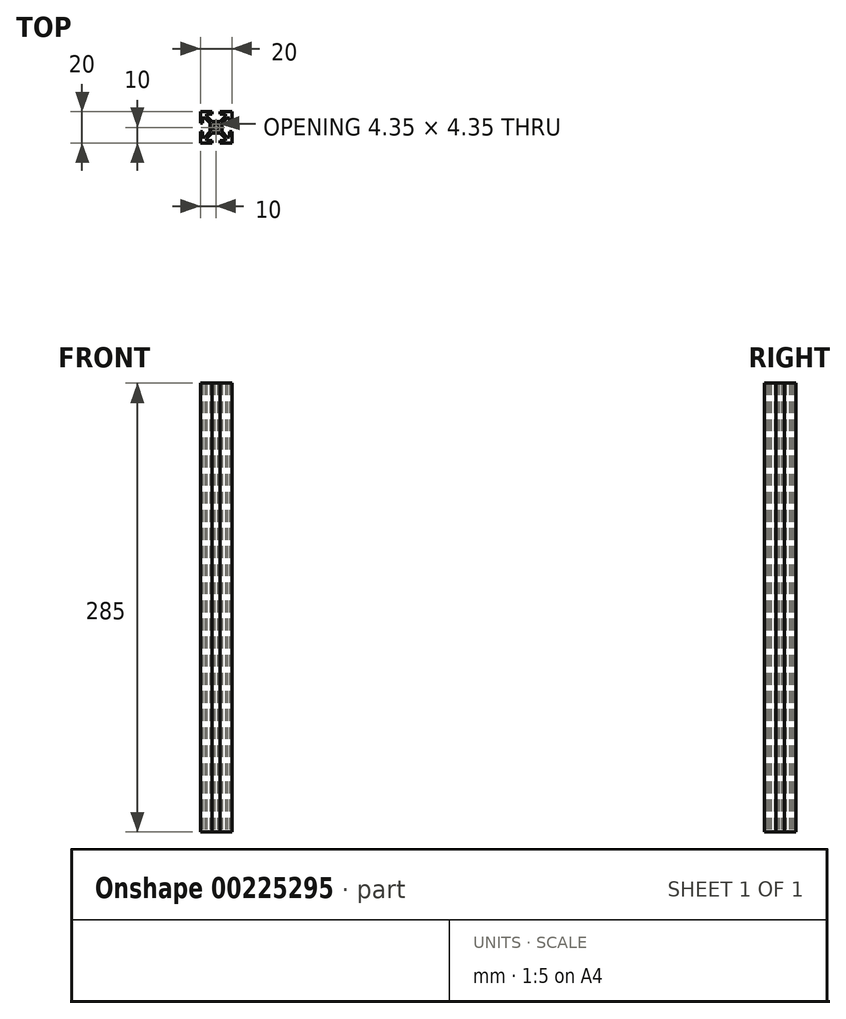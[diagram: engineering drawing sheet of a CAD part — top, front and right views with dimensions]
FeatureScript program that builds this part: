
annotation { "Feature Type Name" : "Feature", "Feature Type Description" : "" }
export const myFeature = defineFeature(function(context is Context, id is Id, definition is map)
    precondition{}
    {
        {
            var Q0;
            Q0=qCreatedBy(makeId("Top.planeOp"),FACE);
            var sketch = newSketch(context, id + "F0", { "sketchPlane" : qUnion([Q0])});
            skLineSegment(sketch, "E0.bottom", {"start": v(10, 10) * mm, "end": v(-10, 10) * mm});
            skLineSegment(sketch, "E0.top", {"start": v(10, -10) * mm, "end": v(-10, -10) * mm});
            skLineSegment(sketch, "E0.left", {"start": v(10, 10) * mm, "end": v(10, -10) * mm});
            skLineSegment(sketch, "E0.right", {"start": v(-10, 10) * mm, "end": v(-10, -10) * mm});
            skPoint(sketch, "E0.middle", {"position": v(0, 0) * mm});
            skLineSegment(sketch, "E1", {"start": v(-10, 10) * mm, "end": v(10, -10) * mm, "construction": true});
            skLineSegment(sketch, "E2", {"start": v(-10, -10) * mm, "end": v(10, 10) * mm, "construction": true});
            skLineSegment(sketch, "E3", {"start": v(0, 10) * mm, "end": v(0, -10) * mm, "construction": true});
            skLineSegment(sketch, "E4", {"start": v(-10, 0) * mm, "end": v(10, 0) * mm, "construction": true});
            skPoint(sketch, "E4.endSnap0", {"position": v(10, 0) * mm});
            skLineSegment(sketch, "E5", {"start": v(-2.63, 13.49) * mm, "end": v(2.63, 13.49) * mm});
            skLineSegment(sketch, "E6", {"start": v(2.63, 13.49) * mm, "end": v(2.63, 8.5) * mm});
            skLineSegment(sketch, "E7", {"start": v(2.63, 8.5) * mm, "end": v(6, 8.5) * mm});
            skLineSegment(sketch, "E8", {"start": v(6, 8.5) * mm, "end": v(6, 7.06) * mm});
            skLineSegment(sketch, "E9", {"start": v(6, 7.06) * mm, "end": v(2.6, 3.66) * mm});
            skLineSegment(sketch, "E10", {"start": v(2.6, 3.66) * mm, "end": v(-2.6, 3.66) * mm});
            skLineSegment(sketch, "E11", {"start": v(-2.6, 3.66) * mm, "end": v(-6, 7.06) * mm});
            skLineSegment(sketch, "E12", {"start": v(-6, 7.06) * mm, "end": v(-6, 8.5) * mm});
            skLineSegment(sketch, "E13", {"start": v(-6, 8.5) * mm, "end": v(-2.63, 8.5) * mm});
            skLineSegment(sketch, "E14", {"start": v(-2.63, 8.5) * mm, "end": v(-2.63, 13.49) * mm});
            skCircle(sketch, "E15", {"center": v(0, 0) * mm, "radius": 2.1 * mm});
            skLineSegment(sketch, "E16.MirrorCS", {"start": v(-7.06, 6) * mm, "end": v(-8.5, 6) * mm});
            skLineSegment(sketch, "E17.MirrorCS", {"start": v(-3.66, 2.6) * mm, "end": v(-7.06, 6) * mm});
            skLineSegment(sketch, "E18.MirrorCS", {"start": v(-8.5, 6) * mm, "end": v(-8.5, 2.63) * mm});
            skLineSegment(sketch, "E19.MirrorCS", {"start": v(-3.66, -2.6) * mm, "end": v(-3.66, 2.6) * mm});
            skLineSegment(sketch, "E20.MirrorCS", {"start": v(-7.06, -6) * mm, "end": v(-3.66, -2.6) * mm});
            skLineSegment(sketch, "E21.MirrorCS", {"start": v(-8.5, -6) * mm, "end": v(-7.06, -6) * mm});
            skLineSegment(sketch, "E22.MirrorCS", {"start": v(-8.5, -2.63) * mm, "end": v(-8.5, -6) * mm});
            skLineSegment(sketch, "E23.MirrorCS", {"start": v(-13.49, -2.63) * mm, "end": v(-8.5, -2.63) * mm});
            skLineSegment(sketch, "E24.MirrorCS", {"start": v(-13.49, 2.63) * mm, "end": v(-13.49, -2.63) * mm});
            skLineSegment(sketch, "E25.MirrorCS", {"start": v(-8.5, 2.63) * mm, "end": v(-13.49, 2.63) * mm});
            skLineSegment(sketch, "E26.MirrorCS", {"start": v(-2.6, -3.66) * mm, "end": v(-6, -7.06) * mm});
            skLineSegment(sketch, "E27.MirrorCS", {"start": v(2.6, -3.66) * mm, "end": v(-2.6, -3.66) * mm});
            skLineSegment(sketch, "E28.MirrorCS", {"start": v(6, -7.06) * mm, "end": v(2.6, -3.66) * mm});
            skLineSegment(sketch, "E29.MirrorCS", {"start": v(6, -8.5) * mm, "end": v(6, -7.06) * mm});
            skLineSegment(sketch, "E30.MirrorCS", {"start": v(2.63, -8.5) * mm, "end": v(6, -8.5) * mm});
            skLineSegment(sketch, "E31.MirrorCS", {"start": v(2.63, -13.49) * mm, "end": v(2.63, -8.5) * mm});
            skLineSegment(sketch, "E32.MirrorCS", {"start": v(-2.63, -13.49) * mm, "end": v(2.63, -13.49) * mm});
            skLineSegment(sketch, "E33.MirrorCS", {"start": v(-2.63, -8.5) * mm, "end": v(-2.63, -13.49) * mm});
            skLineSegment(sketch, "E34.MirrorCS", {"start": v(-6, -8.5) * mm, "end": v(-2.63, -8.5) * mm});
            skLineSegment(sketch, "E35.MirrorCS", {"start": v(-6, -7.06) * mm, "end": v(-6, -8.5) * mm});
            skLineSegment(sketch, "E36.MirrorCS", {"start": v(7.06, 6) * mm, "end": v(3.66, 2.6) * mm});
            skLineSegment(sketch, "E37.MirrorCS", {"start": v(8.5, 6) * mm, "end": v(7.06, 6) * mm});
            skLineSegment(sketch, "E38.MirrorCS", {"start": v(8.5, 2.63) * mm, "end": v(8.5, 6) * mm});
            skLineSegment(sketch, "E39.MirrorCS", {"start": v(13.49, 2.63) * mm, "end": v(8.5, 2.63) * mm});
            skLineSegment(sketch, "E40.MirrorCS", {"start": v(13.49, -2.63) * mm, "end": v(13.49, 2.63) * mm});
            skLineSegment(sketch, "E41.MirrorCS", {"start": v(8.5, -2.63) * mm, "end": v(13.49, -2.63) * mm});
            skLineSegment(sketch, "E42.MirrorCS", {"start": v(8.5, -6) * mm, "end": v(8.5, -2.63) * mm});
            skLineSegment(sketch, "E43.MirrorCS", {"start": v(7.06, -6) * mm, "end": v(8.5, -6) * mm});
            skLineSegment(sketch, "E44.MirrorCS", {"start": v(3.66, -2.6) * mm, "end": v(7.06, -6) * mm});
            skLineSegment(sketch, "E45.MirrorCS", {"start": v(3.66, 2.6) * mm, "end": v(3.66, -2.6) * mm});
            skCircle(sketch, "E46", {"center": v(-1.48, 1.48) * mm, "radius": 0.7 * mm});
            skCircle(sketch, "E47.MirrorC", {"center": v(1.48, 1.48) * mm, "radius": 0.7 * mm});
            skCircle(sketch, "E48.MirrorC", {"center": v(-1.48, -1.48) * mm, "radius": 0.7 * mm});
            skCircle(sketch, "E49.MirrorC", {"center": v(1.48, -1.48) * mm, "radius": 0.7 * mm});
            skSolve(sketch);
        }
        {
            var Q0;
            {var subQ29=sQuery(id+"F0.wireOp",EDGE,"E7");Q0=makeQuery(id+"F0.imprint","IMPRINT",FACE,{"disambiguationData":[TD([[makeQuery(id+"F0.imprint","IMPRINT",EDGE,{"derivedFrom":subQ29}),1.0]])]});}
            extrude(context, id + "F1", {"entities" : qUnion([Q0]), "depth" : 285 * mm});
        }
    });
